# Revit family: Comfort Assist Box CC Round Pan Cistern Mech Soft Close Seat 2111
name_source: partatom
category: Plumbing Fixtures
units: mm (PartAtom-declared; Revit-internal decimal feet)

## family parameters
Always vertical = Yes
Cut with Voids When Loaded = No
Enable Cutting in Views = No
Host = Wall
Maintain Annotation Orientation = No
OmniClass Number = 23.45.00.00
OmniClass Title = Sanitary, Laundry, and Cleaning Equipment
Part Type = Normal
Room Calculation Point = No
Round Connector Dimension = Use Diameter
Shared = No

## types (1)
- Comfort Assist Box CC Round Pan Cistern Mech Soft Close Seat 2111
    Category = Paraplegic / Medical
    Ceramic = White Porcelain
    Colour = White
    Default Elevation = 0 mm  [stored 0 ft]
    Handle = Silver
    Manufacturer = Lecico SA
    Material = Vitreous China
    Model = Comfort Assist Box CC Round Pan Cistern Mech Soft Close Seat 2111
    Plastic clips = White Plastic
    Product Code = COMPARSETROUNBE
    Technical Dimensions = W382 x H846 x D615mm
    URL = https://www.lecicosa.co.za

note: [stored X ft] marks values corroborated as IEEE doubles in the binary element streams (Revit-internal decimal feet)

## geometry (parser evidence)
native form markers: Sweep x3
no freeform markers — native parametric forms only
